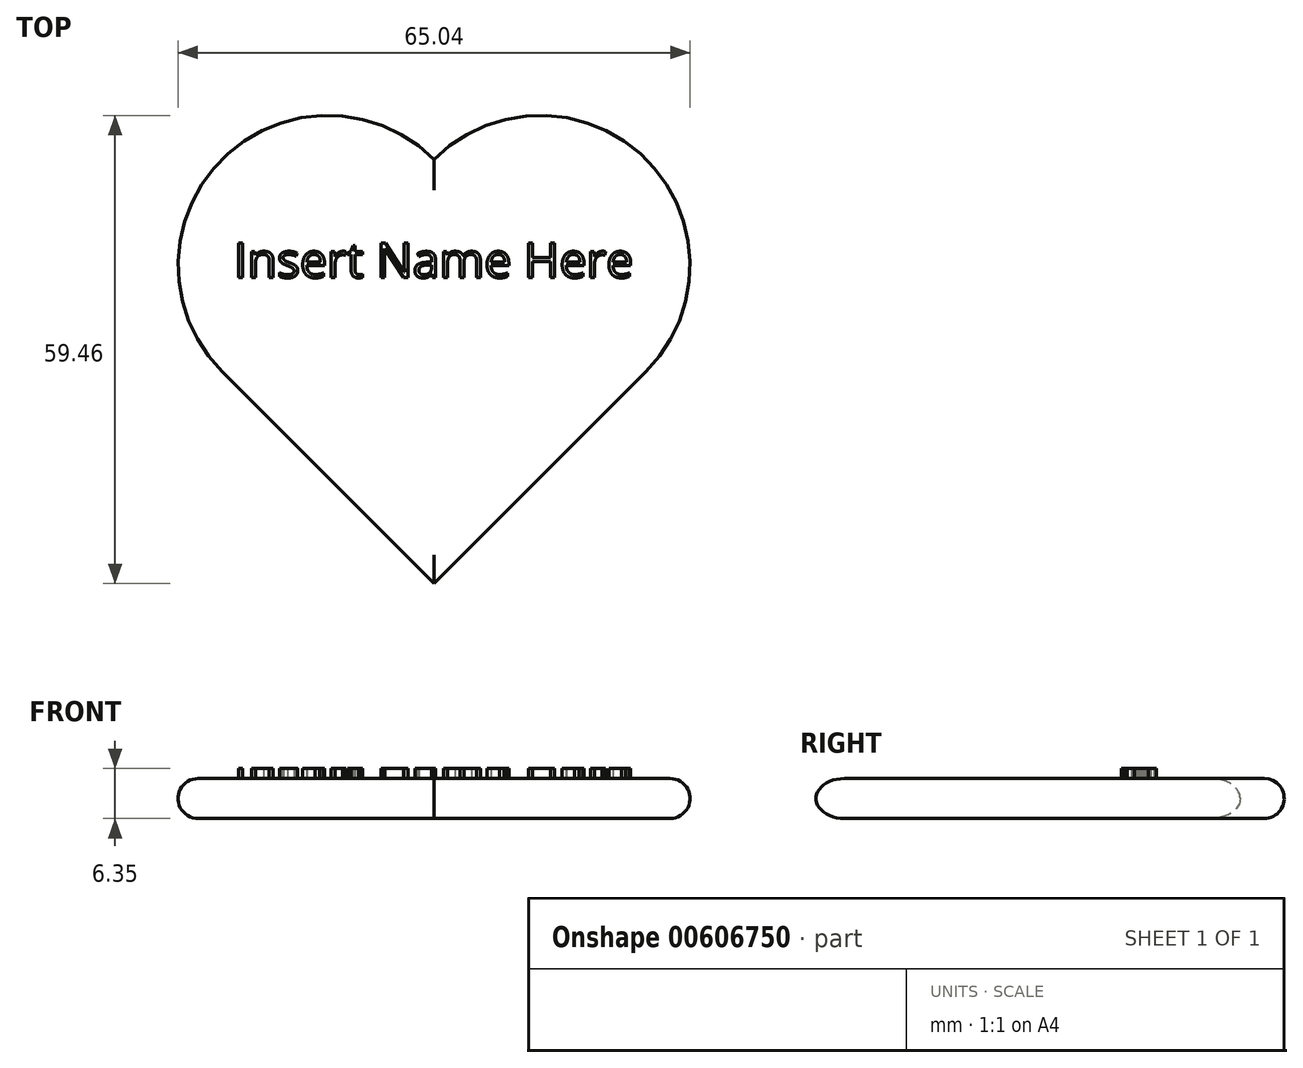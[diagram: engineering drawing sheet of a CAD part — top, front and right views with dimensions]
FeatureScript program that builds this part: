
annotation { "Feature Type Name" : "Feature", "Feature Type Description" : "" }
export const myFeature = defineFeature(function(context is Context, id is Id, definition is map)
    precondition{}
    {
        {
            var Q0;
            Q0=qCreatedBy(makeId("Top.planeOp"),FACE);
            var sketch = newSketch(context, id + "F0", { "sketchPlane" : qUnion([Q0])});
            skLineSegment(sketch, "E0", {"start": v(-40.54, 22.68) * mm, "end": v(-40.54, -15.42) * mm});
            skLineSegment(sketch, "E1", {"start": v(-40.54, -15.42) * mm, "end": v(-2.44, -15.42) * mm});
            skArc(sketch, "E2", {"start": v(-2.44, 22.68) * mm, "mid": v(-21.49, 41.73) * mm, "end": v(-40.54, 22.68) * mm});
            skArc(sketch, "E3", {"start": v(-2.44, -15.42) * mm, "mid": v(16.61, 3.63) * mm, "end": v(-2.44, 22.68) * mm});
            skPoint(sketch, "E4.endSnap0", {"position": v(-21.49, 41.73) * mm});
            skPoint(sketch, "E5.endSnap0", {"position": v(16.61, 3.63) * mm});
            skSolve(sketch);
        }
        {
            var Q0;
            Q0=makeQuery(id+"F0.imprint","IMPRINT",FACE,{"disambiguationData":[TD([[makeQuery(id+"F0.imprint","IMPRINT",EDGE,{"derivedFrom":sQuery(id+"F0.wireOp",EDGE,"E0")}),1.0]])]});
            extrude(context, id + "F1", {"entities" : qUnion([Q0]), "depth" : 5.08 * mm, "offsetDistance" : 25.4 * mm});
        }
        {
            var Q0;
            Q0=makeQuery(id+"F1.opExtrude","SWEPT_BODY",BODY,{"disambiguationData":[OSD([sQuery(id+"F0.wireOp",EDGE,"E0"),sQuery(id+"F0.wireOp",EDGE,"E1"),sQuery(id+"F0.wireOp",EDGE,"E2"),sQuery(id+"F0.wireOp",EDGE,"E3")])]});
            var Q1;
            Q1=makeQuery(id+"F1.opExtrude","SWEPT_EDGE",EDGE,{"disambiguationData":[OSD([sQuery(id+"F0.wireOp",EDGE,"E0"),sQuery(id+"F0.wireOp",EDGE,"E1")])]});
            transform(context, id + "F2", {"entities" : qUnion([Q0]), "transformType" : TransformType.ROTATION, "transformAxis" : qUnion([Q1]), "angle" : 315 * degree, "makeCopy" : false});
        }
        {
            var Q0;
            Q0=makeQuery(id+"F1.opExtrude","CAP_FACE",FACE,{"disambiguationData":[OSD([sQuery(id+"F0.wireOp",EDGE,"E0"),sQuery(id+"F0.wireOp",EDGE,"E1"),sQuery(id+"F0.wireOp",EDGE,"E2"),sQuery(id+"F0.wireOp",EDGE,"E3")])],"isStart":false});
            var sketch = newSketch(context, id + "F3", { "sketchPlane" : qUnion([Q0])});
            skText(sketch, "E6", { "text": "Insert Name Here", "fontName": "OpenSans-Regular.ttf"});
            const initialGuessF3  = {"E6": [-0.06596, 0.02345, 1, 0, 0.00441]};
            skSetInitialGuess(sketch, initialGuessF3);
            skSolve(sketch);
        }
        {
            var Q0;
            Q0 = qSketchRegion(id + "F3", true);
            extrude(context, id + "F4", {"entities" : qUnion([Q0]), "operationType" : NewBodyOperationType.ADD, "depth" : 1.27 * mm, "offsetDistance" : 25.4 * mm});
        }
        {
            var Q0;
            Q0=makeQuery(id+"F1.opExtrude","CAP_EDGE",EDGE,{"disambiguationData":[OSD([sQuery(id+"F0.wireOp",EDGE,"E1")])],"isStart":false});
            var Q1;
            Q1=makeQuery(id+"F1.opExtrude","CAP_EDGE",EDGE,{"disambiguationData":[OSD([sQuery(id+"F0.wireOp",EDGE,"E0")])],"isStart":false});
            var Q2;
            Q2=makeQuery(id+"F1.opExtrude","CAP_FACE",FACE,{"disambiguationData":[OSD([sQuery(id+"F0.wireOp",EDGE,"E0"),sQuery(id+"F0.wireOp",EDGE,"E1"),sQuery(id+"F0.wireOp",EDGE,"E2"),sQuery(id+"F0.wireOp",EDGE,"E3")])],"isStart":true});
            fillet(context, id + "F5", {"entities" : qUnion([Q0, Q1, Q2]), "radius" : 2.54 * mm, "tangentPropagation" : true, "allowEdgeOverflow" : false});
        }
    });
